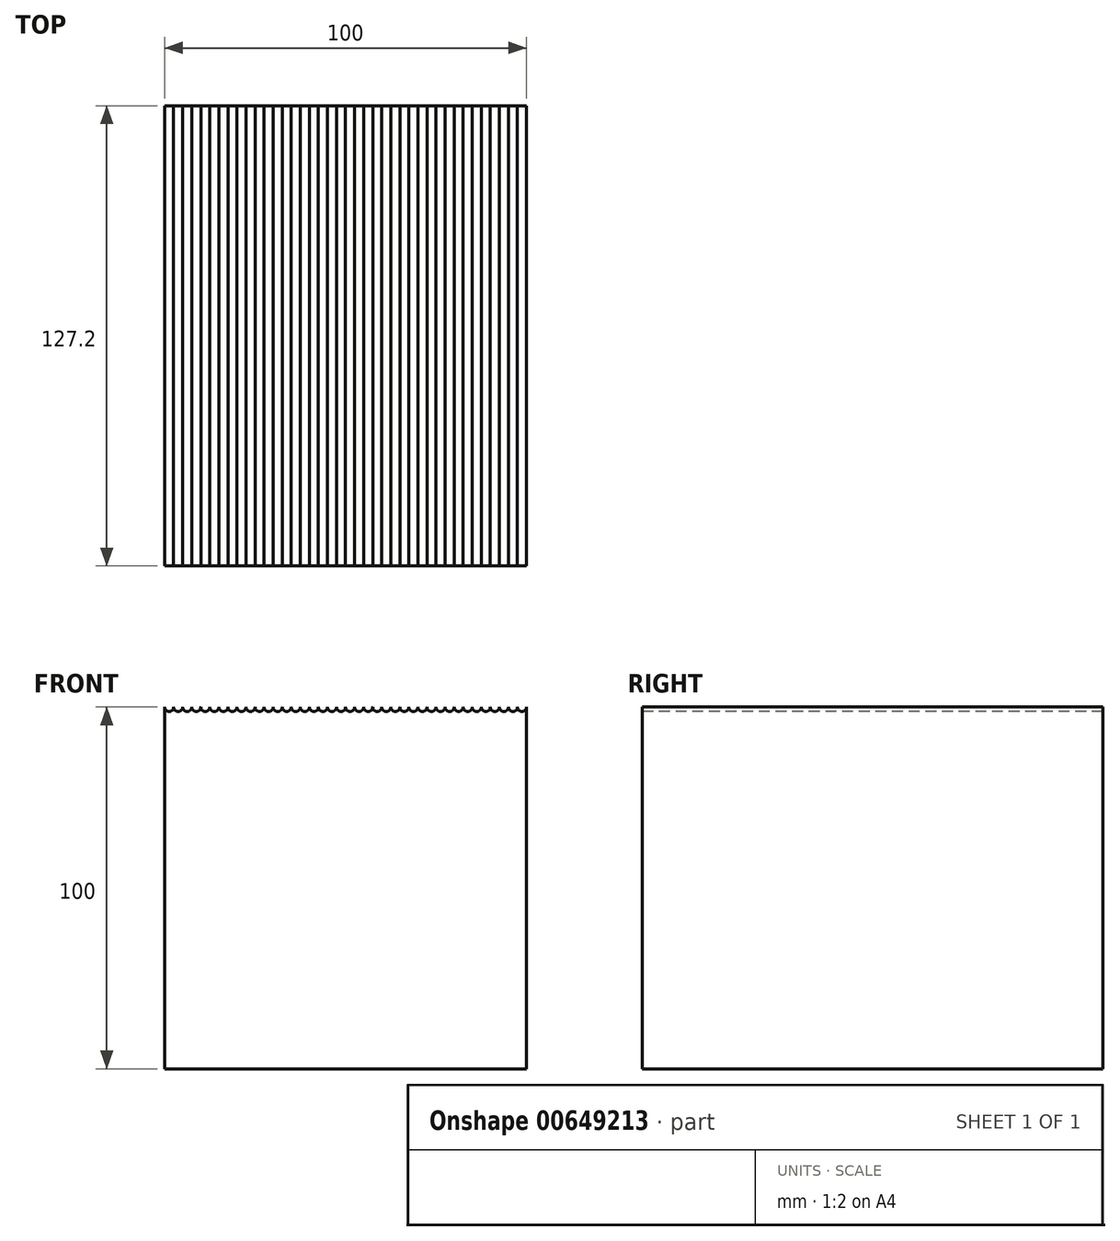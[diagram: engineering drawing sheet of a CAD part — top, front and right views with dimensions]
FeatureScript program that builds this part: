
annotation { "Feature Type Name" : "Feature", "Feature Type Description" : "" }
export const myFeature = defineFeature(function(context is Context, id is Id, definition is map)
    precondition{}
    {
        {
            var Q0;
            Q0=qCreatedBy(makeId("Front.planeOp"),FACE);
            var sketch = newSketch(context, id + "F0", { "sketchPlane" : qUnion([Q0])});
            skLineSegment(sketch, "E0.bottom", {"start": v(50, 50) * mm, "end": v(-50, 50) * mm});
            skLineSegment(sketch, "E0.top", {"start": v(50, -50) * mm, "end": v(-50, -50) * mm});
            skLineSegment(sketch, "E0.left", {"start": v(50, 50) * mm, "end": v(50, -50) * mm});
            skLineSegment(sketch, "E0.right", {"start": v(-50, 50) * mm, "end": v(-50, -50) * mm});
            skPoint(sketch, "E0.middle", {"position": v(0, 0) * mm});
            skSolve(sketch);
        }
        {
            var Q0;
            Q0=makeQuery(id+"F0.imprint","IMPRINT",FACE,{"disambiguationData":[TD([[makeQuery(id+"F0.imprint","IMPRINT",EDGE,{"derivedFrom":sQuery(id+"F0.wireOp",EDGE,"E0.bottom")}),1.0]])]});
            extrude(context, id + "F1", {"entities" : qUnion([Q0]), "endBound" : BoundingType.SYMMETRIC, "depth" : 127.2 * mm, "offsetDistance" : 25 * mm});
        }
        {
            var Q0;
            Q0=makeQuery(id+"F1.opExtrude","CAP_FACE",FACE,{"disambiguationData":[OSD([sQuery(id+"F0.wireOp",EDGE,"E0.bottom"),sQuery(id+"F0.wireOp",EDGE,"E0.top"),sQuery(id+"F0.wireOp",EDGE,"E0.left"),sQuery(id+"F0.wireOp",EDGE,"E0.right")])],"isStart":false});
            var sketch = newSketch(context, id + "F2", { "sketchPlane" : qUnion([Q0])});
            skCircle(sketch, "E1", {"center": v(-48.75, 50) * mm, "radius": 1.25 * mm});
            skCircle(sketch, "E2.1.0.0", {"center": v(-46.25, 50) * mm, "radius": 1.25 * mm});
            skCircle(sketch, "E2.2.0.0", {"center": v(-43.75, 50) * mm, "radius": 1.25 * mm});
            skCircle(sketch, "E2.3.0.0", {"center": v(-41.25, 50) * mm, "radius": 1.25 * mm});
            skCircle(sketch, "E2.4.0.0", {"center": v(-38.75, 50) * mm, "radius": 1.25 * mm});
            skCircle(sketch, "E2.5.0.0", {"center": v(-36.25, 50) * mm, "radius": 1.25 * mm});
            skCircle(sketch, "E2.6.0.0", {"center": v(-33.75, 50) * mm, "radius": 1.25 * mm});
            skCircle(sketch, "E2.7.0.0", {"center": v(-31.25, 50) * mm, "radius": 1.25 * mm});
            skCircle(sketch, "E2.8.0.0", {"center": v(-28.75, 50) * mm, "radius": 1.25 * mm});
            skCircle(sketch, "E2.9.0.0", {"center": v(-26.25, 50) * mm, "radius": 1.25 * mm});
            skCircle(sketch, "E2.10.0.0", {"center": v(-23.75, 50) * mm, "radius": 1.25 * mm});
            skCircle(sketch, "E2.11.0.0", {"center": v(-21.25, 50) * mm, "radius": 1.25 * mm});
            skCircle(sketch, "E2.12.0.0", {"center": v(-18.75, 50) * mm, "radius": 1.25 * mm});
            skCircle(sketch, "E2.13.0.0", {"center": v(-16.25, 50) * mm, "radius": 1.25 * mm});
            skCircle(sketch, "E2.14.0.0", {"center": v(-13.75, 50) * mm, "radius": 1.25 * mm});
            skCircle(sketch, "E2.15.0.0", {"center": v(-11.25, 50) * mm, "radius": 1.25 * mm});
            skCircle(sketch, "E2.16.0.0", {"center": v(-8.75, 50) * mm, "radius": 1.25 * mm});
            skCircle(sketch, "E2.17.0.0", {"center": v(-6.25, 50) * mm, "radius": 1.25 * mm});
            skCircle(sketch, "E2.18.0.0", {"center": v(-3.75, 50) * mm, "radius": 1.25 * mm});
            skCircle(sketch, "E2.19.0.0", {"center": v(-1.25, 50) * mm, "radius": 1.25 * mm});
            skLineSegment(sketch, "E2.direction1", {"start": v(-48.75, 50) * mm, "end": v(-46.25, 50) * mm, "construction": true});
            skCircle(sketch, "E3.0.20.0", {"center": v(1.25, 50) * mm, "radius": 1.25 * mm});
            skCircle(sketch, "E3.0.21.0", {"center": v(3.75, 50) * mm, "radius": 1.25 * mm});
            skCircle(sketch, "E3.0.22.0", {"center": v(6.25, 50) * mm, "radius": 1.25 * mm});
            skCircle(sketch, "E3.0.23.0", {"center": v(8.75, 50) * mm, "radius": 1.25 * mm});
            skCircle(sketch, "E3.0.24.0", {"center": v(11.25, 50) * mm, "radius": 1.25 * mm});
            skCircle(sketch, "E3.0.25.0", {"center": v(13.75, 50) * mm, "radius": 1.25 * mm});
            skCircle(sketch, "E3.0.26.0", {"center": v(16.25, 50) * mm, "radius": 1.25 * mm});
            skCircle(sketch, "E3.0.27.0", {"center": v(18.75, 50) * mm, "radius": 1.25 * mm});
            skCircle(sketch, "E3.0.28.0", {"center": v(21.25, 50) * mm, "radius": 1.25 * mm});
            skCircle(sketch, "E3.0.29.0", {"center": v(23.75, 50) * mm, "radius": 1.25 * mm});
            skCircle(sketch, "E3.0.30.0", {"center": v(26.25, 50) * mm, "radius": 1.25 * mm});
            skCircle(sketch, "E3.0.31.0", {"center": v(28.75, 50) * mm, "radius": 1.25 * mm});
            skCircle(sketch, "E3.0.32.0", {"center": v(31.25, 50) * mm, "radius": 1.25 * mm});
            skCircle(sketch, "E3.0.33.0", {"center": v(33.75, 50) * mm, "radius": 1.25 * mm});
            skCircle(sketch, "E3.0.34.0", {"center": v(36.25, 50) * mm, "radius": 1.25 * mm});
            skCircle(sketch, "E3.0.35.0", {"center": v(38.75, 50) * mm, "radius": 1.25 * mm});
            skCircle(sketch, "E3.0.36.0", {"center": v(41.25, 50) * mm, "radius": 1.25 * mm});
            skCircle(sketch, "E3.0.37.0", {"center": v(43.75, 50) * mm, "radius": 1.25 * mm});
            skCircle(sketch, "E3.0.38.0", {"center": v(46.25, 50) * mm, "radius": 1.25 * mm});
            skCircle(sketch, "E3.0.39.0", {"center": v(48.75, 50) * mm, "radius": 1.25 * mm});
            skSolve(sketch);
        }
        {
            var Q0;
            Q0 = qSketchRegion(id + "F2", true);
            extrude(context, id + "F3", {"entities" : qUnion([Q0]), "operationType" : NewBodyOperationType.REMOVE, "oppositeDirection" : true, "depth" : 144.2 * mm, "offsetDistance" : 25 * mm});
        }
    });
